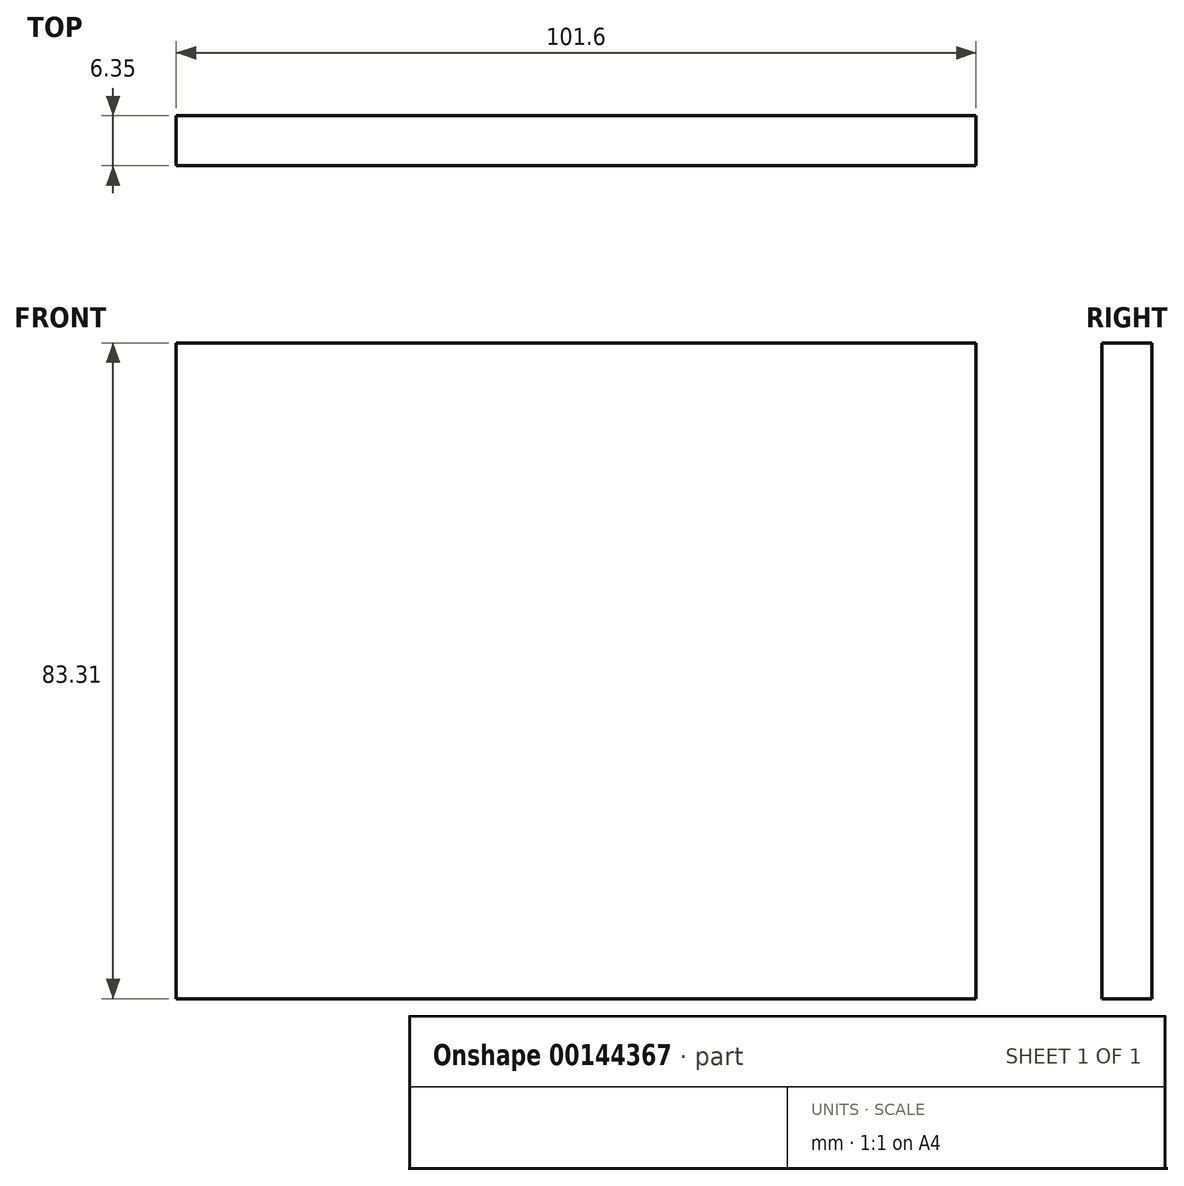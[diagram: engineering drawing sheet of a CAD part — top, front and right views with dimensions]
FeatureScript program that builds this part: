
annotation { "Feature Type Name" : "Feature", "Feature Type Description" : "" }
export const myFeature = defineFeature(function(context is Context, id is Id, definition is map)
    precondition{}
    {
        {
            var Q0;
            Q0=qCreatedBy(makeId("Front.planeOp"),FACE);
            var sketch = newSketch(context, id + "F0", { "sketchPlane" : qUnion([Q0])});
            skLineSegment(sketch, "E0.bottom", {"start": v(0, 0) * mm, "end": v(101.6, 0) * mm});
            skLineSegment(sketch, "E0.top", {"start": v(0, 83.31) * mm, "end": v(101.6, 83.31) * mm});
            skLineSegment(sketch, "E0.left", {"start": v(0, 0) * mm, "end": v(0, 83.31) * mm});
            skLineSegment(sketch, "E0.right", {"start": v(101.6, 0) * mm, "end": v(101.6, 83.31) * mm});
            skSolve(sketch);
        }
        {
            var Q0;
            Q0=makeQuery(id+"F0.imprint","IMPRINT",FACE,{"disambiguationData":[TD([[makeQuery(id+"F0.imprint","IMPRINT",EDGE,{"derivedFrom":sQuery(id+"F0.wireOp",EDGE,"E0.bottom")}),1.0]])]});
            extrude(context, id + "F1", {"entities" : qUnion([Q0]), "depth" : 6.35 * mm});
        }
    });
